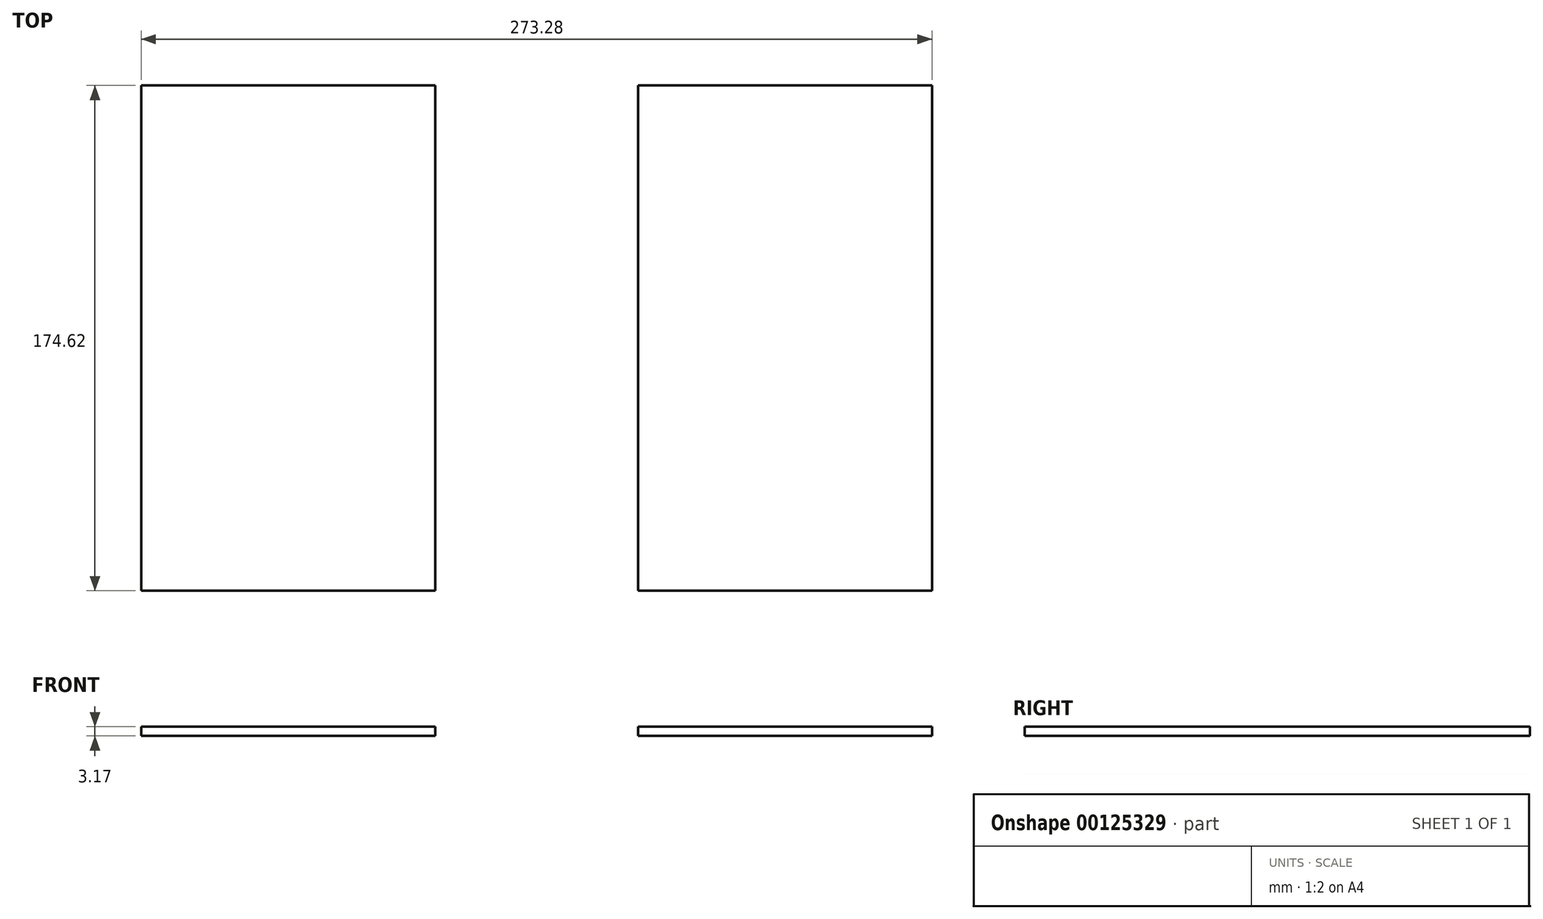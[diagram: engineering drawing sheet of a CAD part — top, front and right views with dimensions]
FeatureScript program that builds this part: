
annotation { "Feature Type Name" : "Feature", "Feature Type Description" : "" }
export const myFeature = defineFeature(function(context is Context, id is Id, definition is map)
    precondition{}
    {
        {
            var Q0;
            Q0=qCreatedBy(makeId("Top.planeOp"),FACE);
            var sketch = newSketch(context, id + "F0", { "sketchPlane" : qUnion([Q0])});
            skLineSegment(sketch, "E0.bottom", {"start": v(50.8, 87.31) * mm, "end": v(-50.8, 87.31) * mm});
            skLineSegment(sketch, "E0.top", {"start": v(50.8, -87.31) * mm, "end": v(-50.8, -87.31) * mm});
            skLineSegment(sketch, "E0.left", {"start": v(50.8, 87.31) * mm, "end": v(50.8, -87.31) * mm});
            skLineSegment(sketch, "E0.right", {"start": v(-50.8, 87.31) * mm, "end": v(-50.8, -87.31) * mm});
            skPoint(sketch, "E0.middle", {"position": v(0, 0) * mm});
            skLineSegment(sketch, "E1.bottom", {"start": v(120.88, 87.31) * mm, "end": v(222.48, 87.31) * mm});
            skLineSegment(sketch, "E1.top", {"start": v(120.88, -87.31) * mm, "end": v(222.48, -87.31) * mm});
            skLineSegment(sketch, "E1.left", {"start": v(120.88, 87.31) * mm, "end": v(120.88, -87.31) * mm});
            skLineSegment(sketch, "E1.right", {"start": v(222.48, 87.31) * mm, "end": v(222.48, -87.31) * mm});
            skPoint(sketch, "E1.middle", {"position": v(171.68, 0) * mm});
            skSolve(sketch);
        }
        {
            var Q0;
            Q0=makeQuery(id+"F0.imprint","IMPRINT",FACE,{"disambiguationData":[TD([[makeQuery(id+"F0.imprint","IMPRINT",EDGE,{"derivedFrom":sQuery(id+"F0.wireOp",EDGE,"E0.bottom")}),1.0]])]});
            extrude(context, id + "F1", {"entities" : qUnion([Q0]), "depth" : 3.17 * mm});
        }
        {
            var Q0;
            Q0=makeQuery(id+"F0.imprint","IMPRINT",FACE,{"disambiguationData":[TD([[makeQuery(id+"F0.imprint","IMPRINT",EDGE,{"derivedFrom":sQuery(id+"F0.wireOp",EDGE,"E1.bottom")}),-1.0]])]});
            extrude(context, id + "F2", {"entities" : qUnion([Q0]), "depth" : 3.17 * mm});
        }
    });
